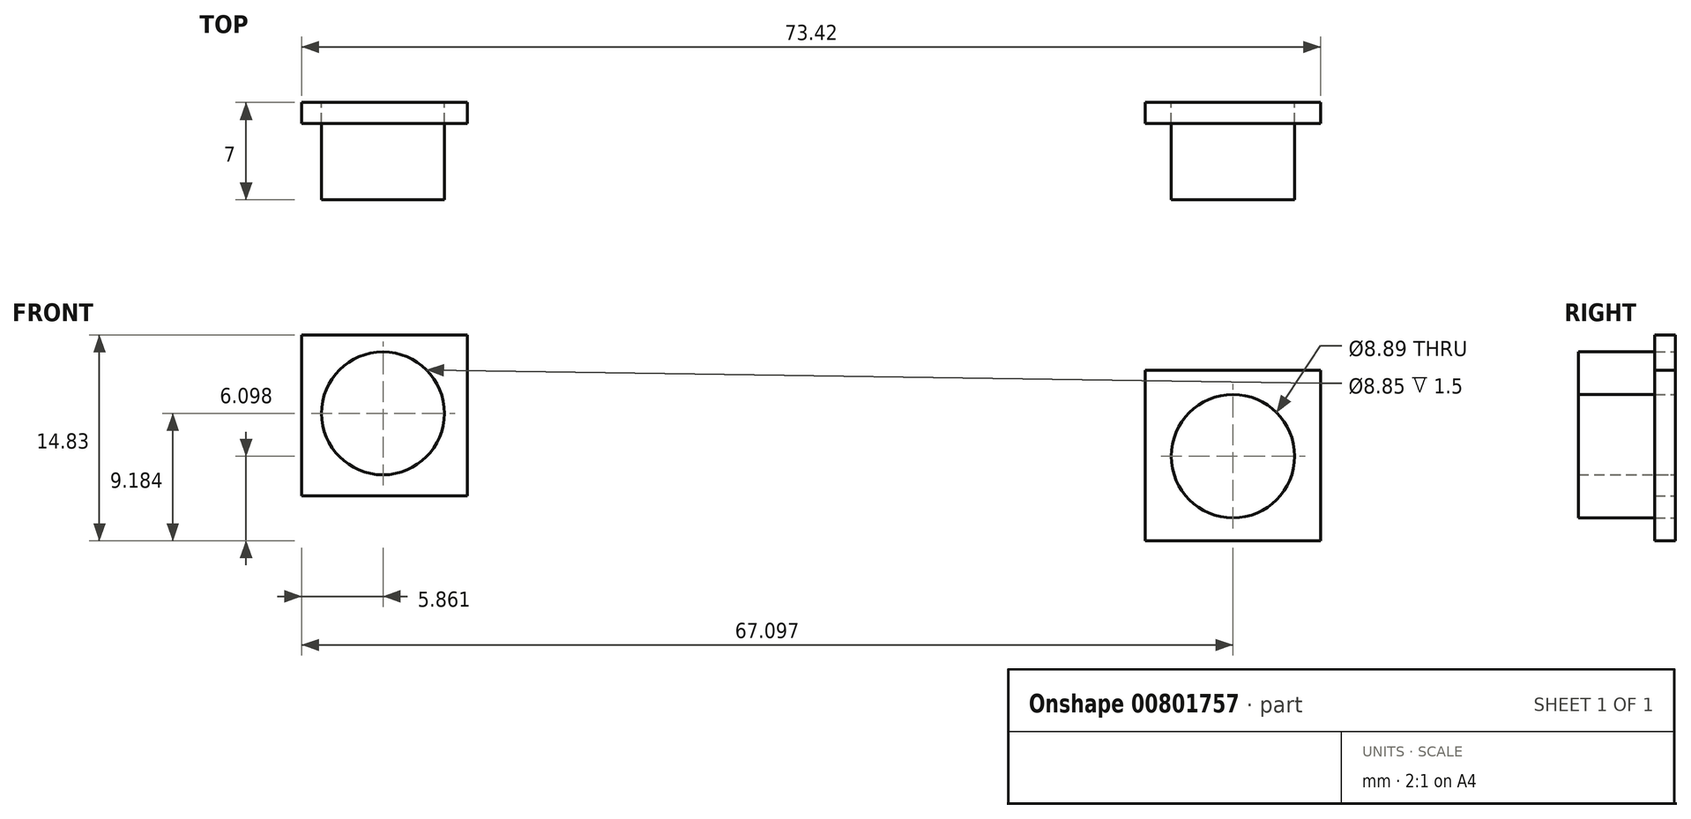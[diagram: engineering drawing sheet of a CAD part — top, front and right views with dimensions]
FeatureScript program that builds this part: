
annotation { "Feature Type Name" : "Feature", "Feature Type Description" : "" }
export const myFeature = defineFeature(function(context is Context, id is Id, definition is map)
    precondition{}
    {
        {
            var Q0;
            Q0=qCreatedBy(makeId("Front.planeOp"),FACE);
            var sketch = newSketch(context, id + "F0", { "sketchPlane" : qUnion([Q0])});
            skCircle(sketch, "E0", {"center": v(-41.43, 31.24) * mm, "radius": 4.43 * mm});
            skCircle(sketch, "E1", {"center": v(19.8, 28.16) * mm, "radius": 4.45 * mm});
            skLineSegment(sketch, "E2.bottom", {"start": v(-47.29, 36.89) * mm, "end": v(-35.35, 36.89) * mm});
            skLineSegment(sketch, "E2.top", {"start": v(-47.29, 25.32) * mm, "end": v(-35.35, 25.32) * mm});
            skLineSegment(sketch, "E2.left", {"start": v(-47.29, 36.89) * mm, "end": v(-47.29, 25.32) * mm});
            skLineSegment(sketch, "E2.right", {"start": v(-35.35, 36.89) * mm, "end": v(-35.35, 25.32) * mm});
            skLineSegment(sketch, "E3.bottom", {"start": v(13.47, 34.36) * mm, "end": v(26.13, 34.36) * mm});
            skLineSegment(sketch, "E3.top", {"start": v(13.47, 22.06) * mm, "end": v(26.13, 22.06) * mm});
            skLineSegment(sketch, "E3.left", {"start": v(13.47, 34.36) * mm, "end": v(13.47, 22.06) * mm});
            skLineSegment(sketch, "E3.right", {"start": v(26.13, 34.36) * mm, "end": v(26.13, 22.06) * mm});
            skSolve(sketch);
        }
        {
            var Q0;
            Q0=makeQuery(id+"F0.imprint","IMPRINT",FACE,{"disambiguationData":[TD([[makeQuery(id+"F0.imprint","IMPRINT",EDGE,{"derivedFrom":sQuery(id+"F0.wireOp",EDGE,"E0")}),1.0]])]});
            var Q1;
            Q1=makeQuery(id+"F0.imprint","IMPRINT",FACE,{"disambiguationData":[TD([[makeQuery(id+"F0.imprint","IMPRINT",EDGE,{"derivedFrom":sQuery(id+"F0.wireOp",EDGE,"E1")}),1.0]])]});
            extrude(context, id + "F1", {"entities" : qUnion([Q0, Q1]), "depth" : 7 * mm, "offsetDistance" : 25 * mm});
        }
        {
            var Q0;
            Q0 = qSketchRegion(id + "F0", true);
            extrude(context, id + "F2", {"entities" : qUnion([Q0]), "depth" : 1.5 * mm, "offsetDistance" : 25 * mm});
        }
    });
